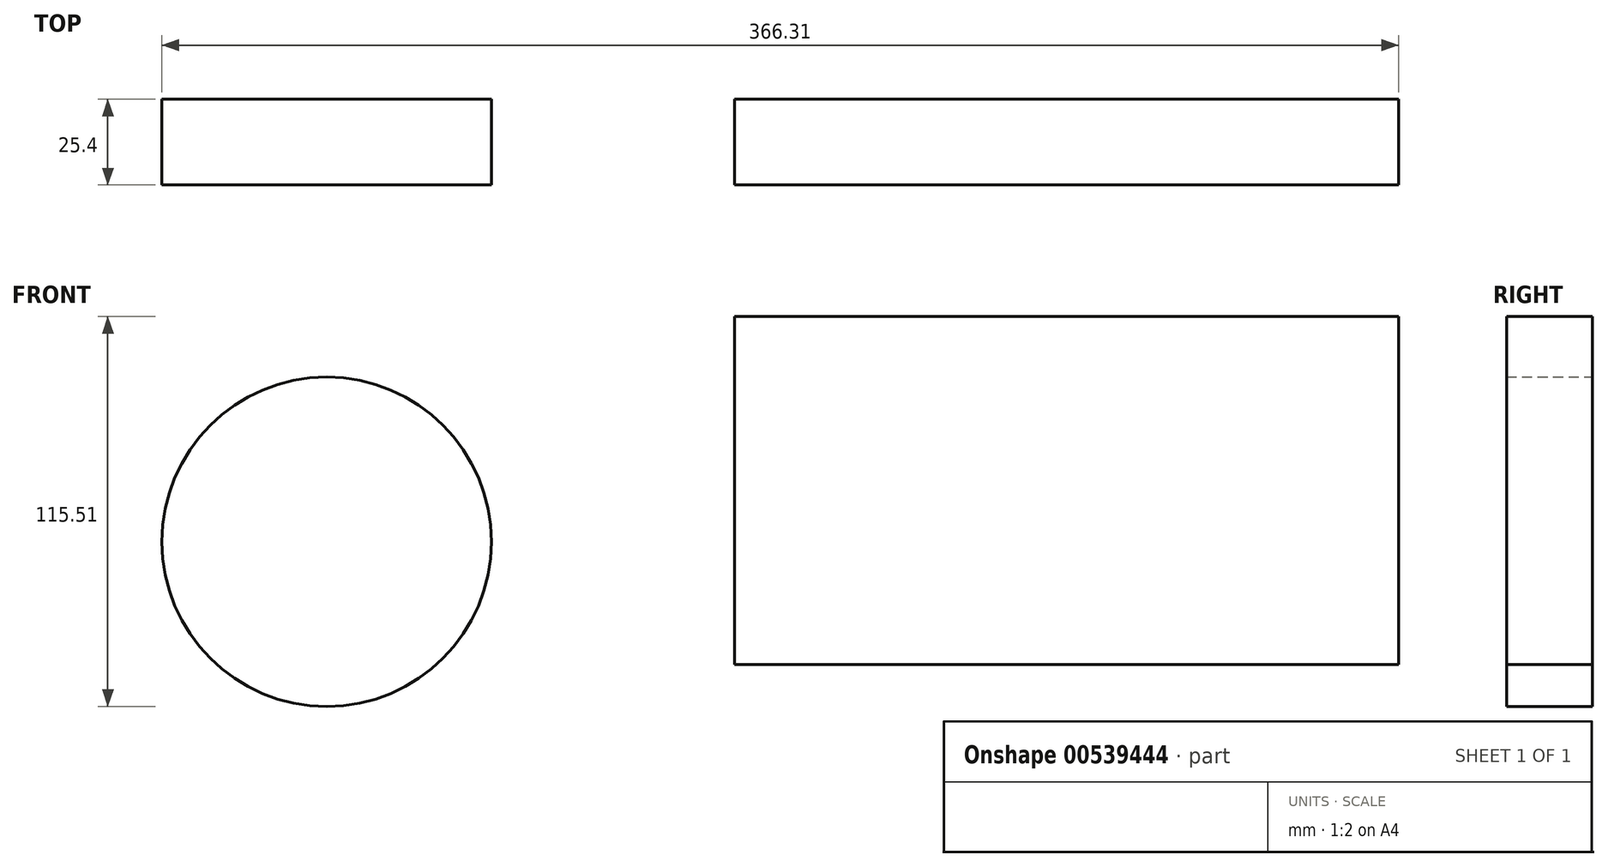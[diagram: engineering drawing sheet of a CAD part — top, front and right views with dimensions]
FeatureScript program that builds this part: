
annotation { "Feature Type Name" : "Feature", "Feature Type Description" : "" }
export const myFeature = defineFeature(function(context is Context, id is Id, definition is map)
    precondition{}
    {
        {
            var Q0;
            Q0=qCreatedBy(makeId("Front.planeOp"),FACE);
            var sketch = newSketch(context, id + "F0", { "sketchPlane" : qUnion([Q0])});
            skLineSegment(sketch, "E0.bottom", {"start": v(98.36, -51.54) * mm, "end": v(-98.36, -51.54) * mm});
            skLineSegment(sketch, "E0.top", {"start": v(98.36, 51.54) * mm, "end": v(-98.36, 51.54) * mm});
            skLineSegment(sketch, "E0.left", {"start": v(98.36, -51.54) * mm, "end": v(98.36, 51.54) * mm});
            skLineSegment(sketch, "E0.right", {"start": v(-98.36, -51.54) * mm, "end": v(-98.36, 51.54) * mm});
            skPoint(sketch, "E0.middle", {"position": v(0, 0) * mm});
            skLineSegment(sketch, "E1.bottom", {"start": v(-98.36, 51.54) * mm, "end": v(-70.04, 51.54) * mm});
            skLineSegment(sketch, "E1.top", {"start": v(-98.36, 24.79) * mm, "end": v(-70.04, 24.79) * mm});
            skLineSegment(sketch, "E1.left", {"start": v(-98.36, 51.54) * mm, "end": v(-98.36, 24.79) * mm});
            skLineSegment(sketch, "E1.right", {"start": v(-70.04, 51.54) * mm, "end": v(-70.04, 24.79) * mm});
            skLineSegment(sketch, "E2.bottom", {"start": v(98.36, 51.54) * mm, "end": v(66.89, 51.54) * mm});
            skLineSegment(sketch, "E2.top", {"start": v(98.36, 24.79) * mm, "end": v(66.89, 24.79) * mm});
            skLineSegment(sketch, "E2.left", {"start": v(98.36, 51.54) * mm, "end": v(98.36, 24.79) * mm});
            skLineSegment(sketch, "E2.right", {"start": v(66.89, 51.54) * mm, "end": v(66.89, 24.79) * mm});
            skLineSegment(sketch, "E3.bottom", {"start": v(-98.36, -51.54) * mm, "end": v(-70.04, -51.54) * mm});
            skLineSegment(sketch, "E3.top", {"start": v(-98.36, -25.57) * mm, "end": v(-70.04, -25.57) * mm});
            skLineSegment(sketch, "E3.left", {"start": v(-98.36, -51.54) * mm, "end": v(-98.36, -25.57) * mm});
            skLineSegment(sketch, "E3.right", {"start": v(-70.04, -51.54) * mm, "end": v(-70.04, -25.57) * mm});
            skLineSegment(sketch, "E4.bottom", {"start": v(98.36, -51.54) * mm, "end": v(66.89, -51.54) * mm});
            skLineSegment(sketch, "E4.top", {"start": v(98.36, -25.57) * mm, "end": v(66.89, -25.57) * mm});
            skLineSegment(sketch, "E4.left", {"start": v(98.36, -51.54) * mm, "end": v(98.36, -25.57) * mm});
            skLineSegment(sketch, "E4.right", {"start": v(66.89, -51.54) * mm, "end": v(66.89, -25.57) * mm});
            skLineSegment(sketch, "E5.bottom", {"start": v(66.89, 24.79) * mm, "end": v(-70.04, 24.79) * mm});
            skLineSegment(sketch, "E5.top", {"start": v(66.89, -25.57) * mm, "end": v(-70.04, -25.57) * mm});
            skLineSegment(sketch, "E5.left", {"start": v(66.89, 24.79) * mm, "end": v(66.89, -25.57) * mm});
            skLineSegment(sketch, "E5.right", {"start": v(-70.04, 24.79) * mm, "end": v(-70.04, -25.57) * mm});
            skLineSegment(sketch, "E6", {"start": v(-264.4, -33.44) * mm, "end": v(-230.57, 32.26) * mm});
            skLineSegment(sketch, "E7", {"start": v(-230.57, 32.26) * mm, "end": v(-173.9, -33.44) * mm});
            skLineSegment(sketch, "E8", {"start": v(-173.9, -33.44) * mm, "end": v(-264.4, -33.44) * mm});
            skCircle(sketch, "E9", {"center": v(-219.15, -15.18) * mm, "radius": 48.8 * mm});
            skSolve(sketch);
        }
        {
            var Q0;
            Q0=makeQuery(id+"F0.imprint","IMPRINT",FACE,{"disambiguationData":[TD([[makeQuery(id+"F0.imprint","IMPRINT",EDGE,{"derivedFrom":sQuery(id+"F0.wireOp",EDGE,"E0.top")}),1.0]])]});
            var Q1;
            Q1=makeQuery(id+"F0.imprint","IMPRINT",FACE,{"disambiguationData":[TD([[makeQuery(id+"F0.imprint","IMPRINT",EDGE,{"derivedFrom":sQuery(id+"F0.wireOp",EDGE,"E1.bottom")}),-1.0]])]});
            var Q2;
            Q2=makeQuery(id+"F0.imprint","IMPRINT",FACE,{"disambiguationData":[TD([[makeQuery(id+"F0.imprint","IMPRINT",EDGE,{"derivedFrom":sQuery(id+"F0.wireOp",EDGE,"E0.right")}),-1.0]])]});
            var Q3;
            Q3=makeQuery(id+"F0.imprint","IMPRINT",FACE,{"disambiguationData":[TD([[makeQuery(id+"F0.imprint","IMPRINT",EDGE,{"derivedFrom":sQuery(id+"F0.wireOp",EDGE,"E5.bottom")}),1.0]])]});
            var Q4;
            Q4=makeQuery(id+"F0.imprint","IMPRINT",FACE,{"disambiguationData":[TD([[makeQuery(id+"F0.imprint","IMPRINT",EDGE,{"derivedFrom":sQuery(id+"F0.wireOp",EDGE,"E2.bottom")}),1.0]])]});
            var Q5;
            Q5=makeQuery(id+"F0.imprint","IMPRINT",FACE,{"disambiguationData":[TD([[makeQuery(id+"F0.imprint","IMPRINT",EDGE,{"derivedFrom":sQuery(id+"F0.wireOp",EDGE,"E0.left")}),1.0]])]});
            var Q6;
            Q6=makeQuery(id+"F0.imprint","IMPRINT",FACE,{"disambiguationData":[TD([[makeQuery(id+"F0.imprint","IMPRINT",EDGE,{"derivedFrom":sQuery(id+"F0.wireOp",EDGE,"E4.bottom")}),-1.0]])]});
            var Q7;
            Q7=makeQuery(id+"F0.imprint","IMPRINT",FACE,{"disambiguationData":[TD([[makeQuery(id+"F0.imprint","IMPRINT",EDGE,{"derivedFrom":sQuery(id+"F0.wireOp",EDGE,"E0.bottom")}),-1.0]])]});
            var Q8;
            Q8=makeQuery(id+"F0.imprint","IMPRINT",FACE,{"disambiguationData":[TD([[makeQuery(id+"F0.imprint","IMPRINT",EDGE,{"derivedFrom":sQuery(id+"F0.wireOp",EDGE,"E3.bottom")}),1.0]])]});
            var Q9;
            {var subQ0=sQuery(id+"F0.wireOp",EDGE,"E6");Q9=makeQuery(id+"F0.imprint","IMPRINT",FACE,{"disambiguationData":[TD([[makeQuery(id+"F0.imprint","IMPRINT",EDGE,{"derivedFrom":subQ0}),1.0]])]});}
            var Q10;
            {var subQ0=sQuery(id+"F0.wireOp",EDGE,"E7");Q10=makeQuery(id+"F0.imprint","IMPRINT",FACE,{"disambiguationData":[TD([[makeQuery(id+"F0.imprint","IMPRINT",EDGE,{"derivedFrom":subQ0}),1.0]])]});}
            var Q11;
            Q11=makeQuery(id+"F0.imprint","IMPRINT",FACE,{"disambiguationData":[TD([[makeQuery(id+"F0.imprint","IMPRINT",EDGE,{"derivedFrom":sQuery(id+"F0.wireOp",EDGE,"E6")}),-1.0]])]});
            var Q12;
            {var subQ0=sQuery(id+"F0.wireOp",EDGE,"E8");Q12=makeQuery(id+"F0.imprint","IMPRINT",FACE,{"disambiguationData":[TD([[makeQuery(id+"F0.imprint","IMPRINT",EDGE,{"derivedFrom":subQ0}),1.0]])]});}
            var Q13;
            Q13 = qConstructionFilter(qBodyType(qCreatedBy(id + "F0" ,EDGE), BodyType.WIRE), ConstructionObject.NO);
            extrude(context, id + "F1", {"entities" : qUnion([Q0, Q1, Q2, Q3, Q4, Q5, Q6, Q7, Q8, Q9, Q10, Q11, Q12]), "surfaceEntities" : qUnion([Q13]), "endBound" : BoundingType.SYMMETRIC, "depth" : 25.4 * mm, "offsetDistance" : 25.4 * mm});
        }
    });
